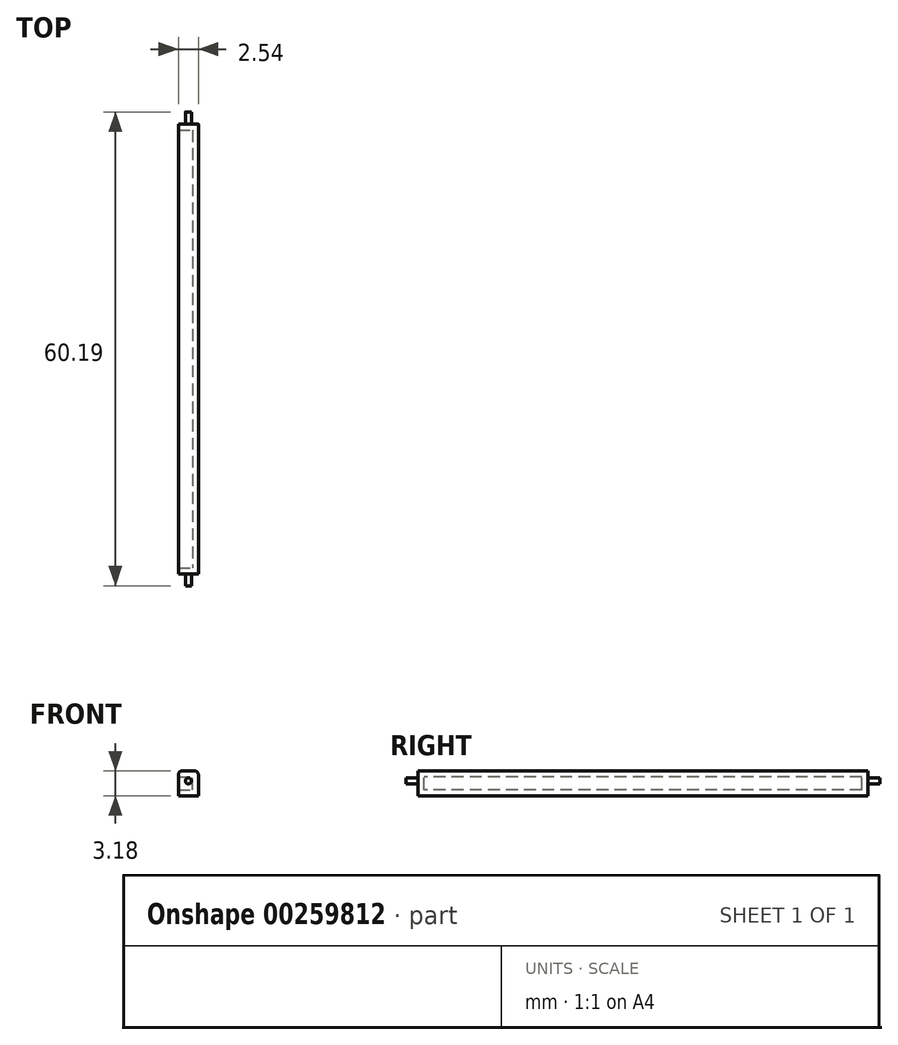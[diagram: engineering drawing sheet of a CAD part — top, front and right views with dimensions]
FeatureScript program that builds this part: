
annotation { "Feature Type Name" : "Feature", "Feature Type Description" : "" }
export const myFeature = defineFeature(function(context is Context, id is Id, definition is map)
    precondition{}
    {
        {
            var Q0;
            Q0=qCreatedBy(makeId("Front.planeOp"),FACE);
            var sketch = newSketch(context, id + "F0", { "sketchPlane" : qUnion([Q0])});
            skLineSegment(sketch, "E0.bottom", {"start": v(-1.27, 0) * mm, "end": v(1.27, 0) * mm});
            skLineSegment(sketch, "E0.top", {"start": v(-0.76, 3.17) * mm, "end": v(0.76, 3.17) * mm});
            skLineSegment(sketch, "E0.left", {"start": v(-1.27, 0) * mm, "end": v(-1.27, 2.67) * mm});
            skLineSegment(sketch, "E0.right", {"start": v(1.27, 0) * mm, "end": v(1.27, 2.67) * mm});
            skPoint(sketch, "E1.visualSharp", {"position": v(-1.27, 3.17) * mm});
            skArc(sketch, "E1.filletArc", {"start": v(-0.76, 3.18) * mm, "mid": v(-1.12, 3.03) * mm, "end": v(-1.27, 2.67) * mm});
            skPoint(sketch, "E2.visualSharp", {"position": v(1.27, 3.17) * mm});
            skArc(sketch, "E2.filletArc", {"start": v(1.27, 2.67) * mm, "mid": v(1.12, 3.03) * mm, "end": v(0.76, 3.18) * mm});
            skSolve(sketch);
        }
        {
            var Q0;
            Q0=qSketchRegion(id+"F0",true);
            extrude(context, id + "F1", {"entities" : qUnion([Q0]), "oppositeDirection" : true, "depth" : 57.15 * mm});
        }
        {
            var Q0;
            Q0=makeQuery(id+"F1.opExtrude","CAP_FACE",FACE,{"disambiguationData":[OSD([sQuery(id+"F0.wireOp",EDGE,"E0.bottom"),sQuery(id+"F0.wireOp",EDGE,"E0.top"),sQuery(id+"F0.wireOp",EDGE,"E0.left"),sQuery(id+"F0.wireOp",EDGE,"E0.right"),sQuery(id+"F0.wireOp",EDGE,"E1.filletArc"),sQuery(id+"F0.wireOp",EDGE,"E2.filletArc")])],"isStart":true});
            var sketch = newSketch(context, id + "F2", { "sketchPlane" : qUnion([Q0])});
            skCircle(sketch, "E3", {"center": v(0, 1.9) * mm, "radius": 0.38 * mm});
            skSolve(sketch);
        }
        {
            var Q0;
            Q0=qSketchRegion(id+"F2",true);
            extrude(context, id + "F3", {"entities" : qUnion([Q0]), "operationType" : NewBodyOperationType.ADD, "depth" : 1.52 * mm});
        }
        {
            var Q0;
            Q0=makeQuery(id+"F1.opExtrude","CAP_FACE",FACE,{"disambiguationData":[OSD([sQuery(id+"F0.wireOp",EDGE,"E0.bottom"),sQuery(id+"F0.wireOp",EDGE,"E0.top"),sQuery(id+"F0.wireOp",EDGE,"E0.left"),sQuery(id+"F0.wireOp",EDGE,"E0.right"),sQuery(id+"F0.wireOp",EDGE,"E1.filletArc"),sQuery(id+"F0.wireOp",EDGE,"E2.filletArc")])],"isStart":false});
            var sketch = newSketch(context, id + "F4", { "sketchPlane" : qUnion([Q0])});
            skCircle(sketch, "E4", {"center": v(0, 1.9) * mm, "radius": 0.38 * mm});
            skSolve(sketch);
        }
        {
            var Q0;
            Q0=qSketchRegion(id+"F4",true);
            extrude(context, id + "F5", {"entities" : qUnion([Q0]), "operationType" : NewBodyOperationType.ADD, "depth" : 1.52 * mm});
        }
        {
            var Q0;
            Q0=makeQuery(id+"F1.opExtrude","SWEPT_FACE",FACE,{"disambiguationData":[OSD([sQuery(id+"F0.wireOp",EDGE,"E0.left")])]});
            shell(context, id + "F6", {"entities" : qUnion([Q0]), "thickness" : 0.76 * mm});
        }
    });
